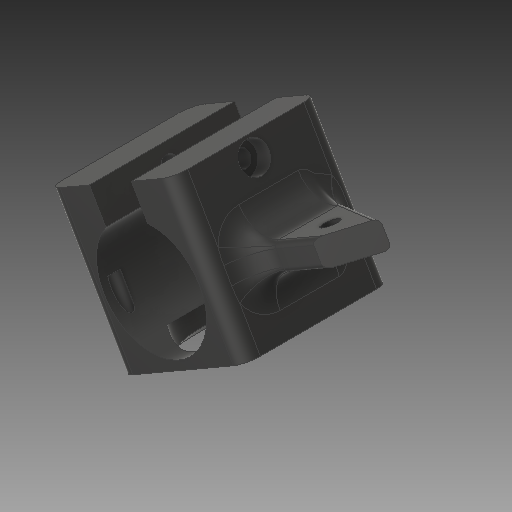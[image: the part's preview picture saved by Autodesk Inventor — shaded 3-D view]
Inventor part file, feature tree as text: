
AUTODESK INVENTOR PART (.ipt)
format: ipt  version: 2019 (Build 230136000, 136)  size: 739,840 bytes
history: native  units: mm
features: other x3, sketch x1, plane x1
ambient origin geometry x8: Origin, YZ Plane, XZ Plane, XY Plane, X Axis, Y Axis, Z Axis, Center Point
bodies: Solid1 (feature_tree)
feature tree (5):
  other  "Heatsink_Fan_Fan Right.ipt"
  other  "Solid1::Heatsink_Fan_Fan Right.ipt"
  other  "TaggingFeature1"
  sketch  "Sketch1"  dims[d0=10.0mm]
  plane  "Work Plane1"
